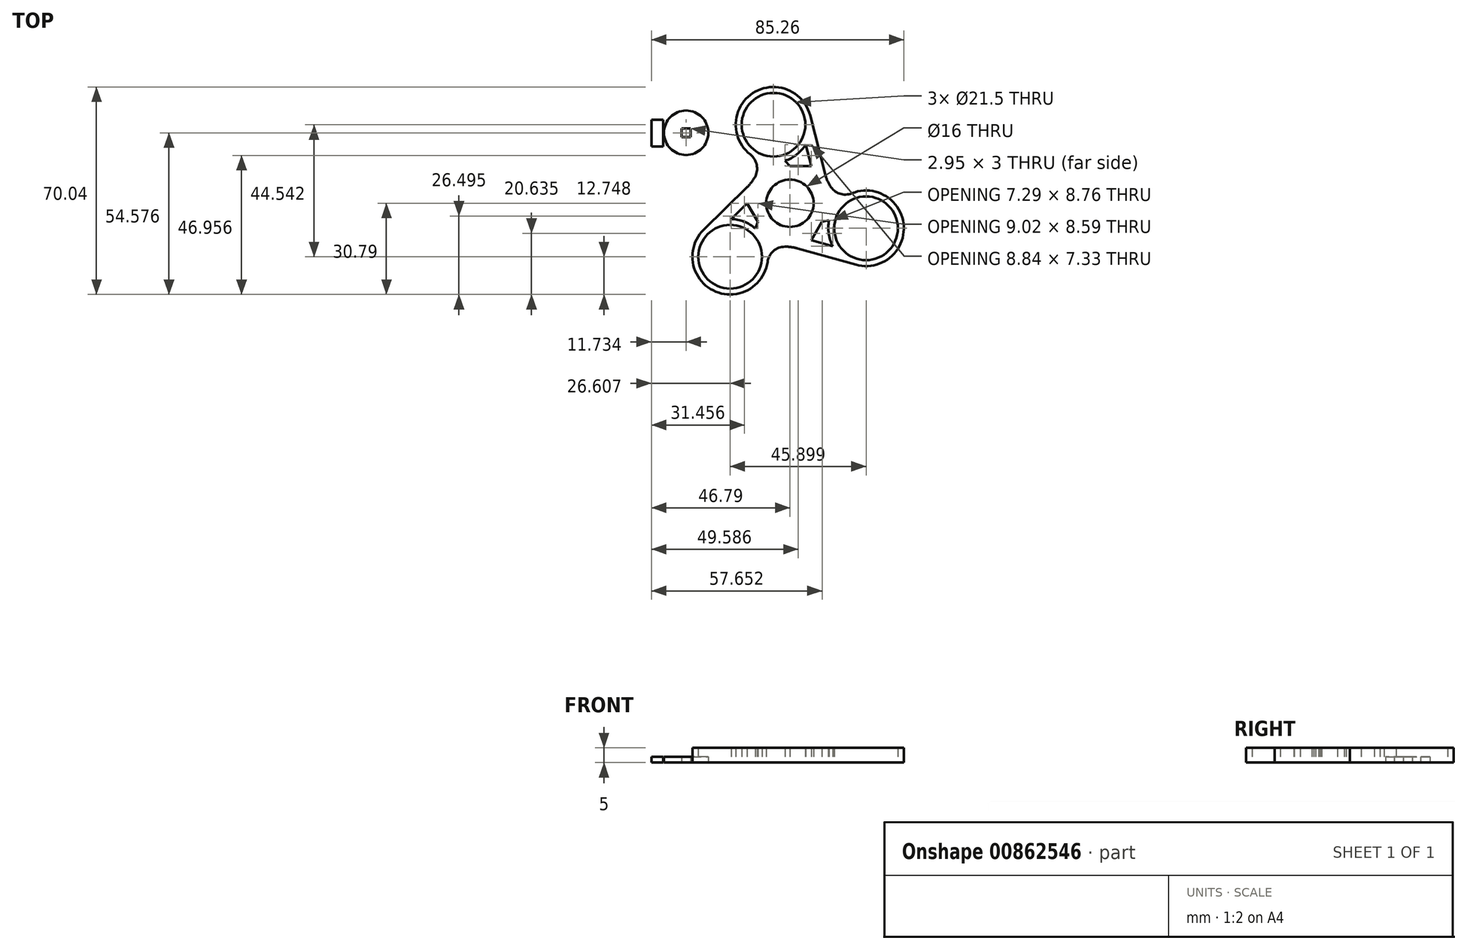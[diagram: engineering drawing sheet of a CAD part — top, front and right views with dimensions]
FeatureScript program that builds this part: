
annotation { "Feature Type Name" : "Feature", "Feature Type Description" : "" }
export const myFeature = defineFeature(function(context is Context, id is Id, definition is map)
    precondition{}
    {
        {
            var Q0;
            Q0=qCreatedBy(makeId("Top.planeOp"),FACE);
            var sketch = newSketch(context, id + "F0", { "sketchPlane" : qUnion([Q0])});
            skCircle(sketch, "E0", {"center": v(0, 0) * mm, "radius": 8 * mm});
            skCircle(sketch, "E1.cCircle", {"center": v(0, 0) * mm, "radius": 12.5 * mm, "construction": true});
            skLineSegment(sketch, "E1.0", {"start": v(-7.22, 12.5) * mm, "end": v(7.22, 12.5) * mm});
            skLineSegment(sketch, "E1.1", {"start": v(7.22, 12.5) * mm, "end": v(14.43, 0) * mm});
            skLineSegment(sketch, "E1.2", {"start": v(14.43, 0) * mm, "end": v(7.22, -12.5) * mm});
            skLineSegment(sketch, "E1.3", {"start": v(7.22, -12.5) * mm, "end": v(-7.22, -12.5) * mm});
            skLineSegment(sketch, "E1.4", {"start": v(-7.22, -12.5) * mm, "end": v(-14.43, 0) * mm});
            skLineSegment(sketch, "E1.5", {"start": v(-14.43, 0) * mm, "end": v(-7.22, 12.5) * mm});
            skPoint(sketch, "E1.0.midPoint", {"position": v(0, 12.5) * mm});
            skLineSegment(sketch, "E2", {"start": v(7.22, 12.5) * mm, "end": v(7.22, 26.5) * mm, "construction": true});
            skArc(sketch, "E3", {"start": v(7.22, 26.5) * mm, "mid": v(-12.8, 36.98) * mm, "end": v(-10, 14.56) * mm});
            skLineSegment(sketch, "E4", {"start": v(-10, 14.56) * mm, "end": v(-7.22, 12.5) * mm});
            skCircle(sketch, "E5", {"center": v(-5.53, 26.5) * mm, "radius": 10.75 * mm});
            skLineSegment(sketch, "E6", {"start": v(14.43, 0) * mm, "end": v(6.82, 29.67) * mm});
            skArc(sketch, "E7", {"start": v(-1.62, 14.36) * mm, "mid": v(2.34, 16.47) * mm, "end": v(5.33, 19.83) * mm});
            skLineSegment(sketch, "E8", {"start": v(-1.62, 14.36) * mm, "end": v(0, 12.5) * mm});
            skLineSegment(sketch, "E9", {"start": v(5.33, 19.83) * mm, "end": v(7.22, 12.5) * mm});
            skSolve(sketch);
        }
        {
            var Q0;
            Q0=makeQuery(id+"F0.imprint","IMPRINT",FACE,{"disambiguationData":[TD([[makeQuery(id+"F0.imprint","IMPRINT",EDGE,{"derivedFrom":sQuery(id+"F0.wireOp",EDGE,"E0")}),-1.0]])]});
            extrude(context, id + "F1", {"entities" : qUnion([Q0]), "depth" : 5 * mm, "offsetDistance" : 25 * mm});
        }
        {
            var Q0;
            Q0=makeQuery(id+"F0.imprint","IMPRINT",FACE,{"disambiguationData":[TD([[makeQuery(id+"F0.imprint","IMPRINT",EDGE,{"derivedFrom":sQuery(id+"F0.wireOp",EDGE,"320d77fd-baf2-4bbf-b8b8-08af1715379d.0")}),1.0]])]});
            var Q1;
            {var subQ0=sQuery(id+"F0.wireOp",EDGE,"f425258b-878d-4473-b1fe-abe1052e9d06.2");var subQ1=sQuery(id+"F0.wireOp",EDGE,"f425258b-878d-4473-b1fe-abe1052e9d06.cCircle");var subQ2=makeQuery(id+"F0.imprint","INTERSECT",VERTEX,{"derivedFrom":[subQ1,subQ0]});Q1=makeQuery(id+"F0.imprint","IMPRINT",FACE,{"disambiguationData":[TD([[makeQuery(id+"F0.imprint","IMPRINT",EDGE,{"disambiguationData":[TD([[subQ2,1.0]])],"derivedFrom":subQ1}),-1.0]])]});}
            var Q2;
            {var subQ0=sQuery(id+"F0.wireOp",EDGE,"f425258b-878d-4473-b1fe-abe1052e9d06.4");var subQ1=sQuery(id+"F0.wireOp",EDGE,"f425258b-878d-4473-b1fe-abe1052e9d06.cCircle");var subQ2=makeQuery(id+"F0.imprint","INTERSECT",VERTEX,{"derivedFrom":[subQ1,subQ0]});Q2=makeQuery(id+"F0.imprint","IMPRINT",FACE,{"disambiguationData":[TD([[makeQuery(id+"F0.imprint","IMPRINT",EDGE,{"disambiguationData":[TD([[subQ2,-1.0]])],"derivedFrom":subQ1}),-1.0]])]});}
            var Q3;
            Q3=makeQuery(id+"F0.imprint","IMPRINT",FACE,{"disambiguationData":[TD([[makeQuery(id+"F0.imprint","IMPRINT",EDGE,{"derivedFrom":sQuery(id+"F0.wireOp",EDGE,"E1.1")}),1.0]])]});
            extrude(context, id + "F2", {"entities" : qUnion([Q0, Q1, Q2, Q3]), "depth" : 5 * mm, "offsetDistance" : 25 * mm});
        }
        {
            var Q0;
            Q0=makeQuery(id+"F2.opExtrude","SWEPT_BODY",BODY,{"disambiguationData":[OSD([sQuery(id+"F0.wireOp",EDGE,"f425258b-878d-4473-b1fe-abe1052e9d06.0"),sQuery(id+"F0.wireOp",EDGE,"f425258b-878d-4473-b1fe-abe1052e9d06.1"),sQuery(id+"F0.wireOp",EDGE,"f425258b-878d-4473-b1fe-abe1052e9d06.2"),sQuery(id+"F0.wireOp",EDGE,"f425258b-878d-4473-b1fe-abe1052e9d06.3"),sQuery(id+"F0.wireOp",EDGE,"f425258b-878d-4473-b1fe-abe1052e9d06.4"),sQuery(id+"F0.wireOp",EDGE,"f425258b-878d-4473-b1fe-abe1052e9d06.5"),sQuery(id+"F0.wireOp",EDGE,"320d77fd-baf2-4bbf-b8b8-08af1715379d.0"),sQuery(id+"F0.wireOp",EDGE,"320d77fd-baf2-4bbf-b8b8-08af1715379d.1"),sQuery(id+"F0.wireOp",EDGE,"320d77fd-baf2-4bbf-b8b8-08af1715379d.2"),sQuery(id+"F0.wireOp",EDGE,"320d77fd-baf2-4bbf-b8b8-08af1715379d.3"),sQuery(id+"F0.wireOp",EDGE,"320d77fd-baf2-4bbf-b8b8-08af1715379d.4"),sQuery(id+"F0.wireOp",EDGE,"320d77fd-baf2-4bbf-b8b8-08af1715379d.5")])]});
            var Q1;
            Q1=makeQuery(id+"F2.opExtrude","SWEPT_BODY",BODY,{"disambiguationData":[OSD([sQuery(id+"F0.wireOp",EDGE,"E1.0"),sQuery(id+"F0.wireOp",EDGE,"E2"),sQuery(id+"F0.wireOp",EDGE,"E3"),sQuery(id+"F0.wireOp",EDGE,"E4"),sQuery(id+"F0.wireOp",EDGE,"E5")])]});
            var Q2;
            Q2=sQuery(id+"F0.wireOp",EDGE,"E1.cCircle");
            circularPattern(context, id + "F3", {"operationType" : NewBodyOperationType.ADD, "entities" : qUnion([Q0, Q1]), "axis" : qUnion([Q2]), "angle" : 360 * degree, "instanceCount" : 3, "equalSpace" : true});
        }
        {
            var Q0;
            Q0=makeQuery(id+"F3.boolean.opBoolean","MERGE",EDGE,{"derivedFrom":[makeQuery(id+"F1.opExtrude","SWEPT_EDGE",EDGE,{"disambiguationData":[OSD([sQuery(id+"F0.wireOp",EDGE,"E1.3"),sQuery(id+"F0.wireOp",EDGE,"E1.4")])]}),makeQuery(id+"F3.opPattern","COPY",EDGE,{"derivedFrom":makeQuery(id+"F2.opExtrude","SWEPT_EDGE",EDGE,{"disambiguationData":[OSD([sQuery(id+"F0.wireOp",EDGE,"E1.0"),sQuery(id+"F0.wireOp",EDGE,"E1.5"),sQuery(id+"F0.wireOp",EDGE,"E4")])]}),"instanceName":"1"})]});
            var Q1;
            {var subQ0=sQuery(id+"F0.wireOp",EDGE,"E4");var subQ1=sQuery(id+"F0.wireOp",EDGE,"E1.5");var subQ2=sQuery(id+"F0.wireOp",EDGE,"E1.0");Q1=makeQuery(id+"F3.boolean.opBoolean","MERGE",EDGE,{"derivedFrom":[makeQuery(id+"F1.opExtrude","SWEPT_EDGE",EDGE,{"disambiguationData":[OSD([subQ2,subQ1,subQ0])]}),makeQuery(id+"F2.opExtrude","SWEPT_EDGE",EDGE,{"disambiguationData":[OSD([subQ2,subQ1,subQ0])]})]});}
            var Q2;
            Q2=makeQuery(id+"F3.boolean.opBoolean","MERGE",EDGE,{"derivedFrom":[makeQuery(id+"F1.opExtrude","SWEPT_EDGE",EDGE,{"disambiguationData":[OSD([sQuery(id+"F0.wireOp",EDGE,"E1.1"),sQuery(id+"F0.wireOp",EDGE,"E1.2")])]}),makeQuery(id+"F3.opPattern","COPY",EDGE,{"derivedFrom":makeQuery(id+"F2.opExtrude","SWEPT_EDGE",EDGE,{"disambiguationData":[OSD([sQuery(id+"F0.wireOp",EDGE,"E1.0"),sQuery(id+"F0.wireOp",EDGE,"E1.5"),sQuery(id+"F0.wireOp",EDGE,"E4")])]}),"instanceName":"2"})]});
            fillet(context, id + "F4", {"entities" : qUnion([Q0, Q1, Q2]), "radius" : 15 * mm, "tangentPropagation" : true, "allowEdgeOverflow" : false});
        }
        {
            var Q0;
            Q0=qCreatedBy(makeId("Top.planeOp"),FACE);
            var sketch = newSketch(context, id + "F5", { "sketchPlane" : qUnion([Q0])});
            skCircle(sketch, "E10", {"center": v(-44.8, 15.18) * mm, "radius": 2.5 * mm, "construction": true});
            skLineSegment(sketch, "E11.bottom", {"start": v(-46.8, 16.68) * mm, "end": v(-42.8, 16.68) * mm});
            skLineSegment(sketch, "E11.top", {"start": v(-46.8, 13.68) * mm, "end": v(-42.8, 13.68) * mm});
            skLineSegment(sketch, "E11.left", {"start": v(-46.8, 16.68) * mm, "end": v(-46.8, 13.68) * mm});
            skLineSegment(sketch, "E11.right", {"start": v(-42.8, 16.68) * mm, "end": v(-42.8, 13.68) * mm});
            skLineSegment(sketch, "E12.bottom", {"start": v(-46.8, 19.18) * mm, "end": v(-42.8, 19.18) * mm});
            skLineSegment(sketch, "E12.top", {"start": v(-46.8, 28.18) * mm, "end": v(-42.8, 28.18) * mm});
            skLineSegment(sketch, "E12.left", {"start": v(-46.8, 19.18) * mm, "end": v(-46.8, 28.18) * mm});
            skLineSegment(sketch, "E12.right", {"start": v(-42.8, 19.18) * mm, "end": v(-42.8, 28.18) * mm});
            skPoint(sketch, "E12.middle", {"position": v(-44.8, 23.68) * mm});
            skCircle(sketch, "E13", {"center": v(-35.06, 23.79) * mm, "radius": 7.5 * mm});
            skLineSegment(sketch, "E14.bottom", {"start": v(-36.53, 25.29) * mm, "end": v(-33.58, 25.29) * mm});
            skLineSegment(sketch, "E14.top", {"start": v(-36.53, 22.29) * mm, "end": v(-33.58, 22.29) * mm});
            skLineSegment(sketch, "E14.left", {"start": v(-36.53, 25.29) * mm, "end": v(-36.53, 22.29) * mm});
            skLineSegment(sketch, "E14.right", {"start": v(-33.58, 25.29) * mm, "end": v(-33.58, 22.29) * mm});
            skSolve(sketch);
        }
        {
            var Q0;
            Q0=makeQuery(id+"F5.imprint","IMPRINT",FACE,{"disambiguationData":[TD([[makeQuery(id+"F5.imprint","IMPRINT",EDGE,{"derivedFrom":sQuery(id+"F5.wireOp",EDGE,"E12.bottom")}),1.0]])]});
            var Q1;
            Q1=makeQuery(id+"F5.imprint","IMPRINT",FACE,{"disambiguationData":[TD([[makeQuery(id+"F5.imprint","IMPRINT",EDGE,{"derivedFrom":sQuery(id+"F5.wireOp",EDGE,"E13")}),1.0]])]});
            extrude(context, id + "F6", {"entities" : qUnion([Q0, Q1]), "depth" : 2 * mm, "offsetDistance" : 25 * mm});
        }
        {
            var Q0;
            {var subQ0=sQuery(id+"F0.wireOp",EDGE,"E4");var subQ1=sQuery(id+"F0.wireOp",EDGE,"E1.5");var subQ2=sQuery(id+"F0.wireOp",EDGE,"E1.0");Q0=makeQuery(id+"F4.opFillet","BLEND_EDGE",EDGE,{"blendedFrom":[makeQuery(id+"F3.boolean.opBoolean","MERGE",EDGE,{"derivedFrom":[makeQuery(id+"F1.opExtrude","SWEPT_EDGE",EDGE,{"disambiguationData":[OSD([subQ2,subQ1,subQ0])]}),makeQuery(id+"F2.opExtrude","SWEPT_EDGE",EDGE,{"disambiguationData":[OSD([subQ2,subQ1,subQ0])]})]}),makeQuery(id+"F2.opExtrude","SWEPT_FACE",FACE,{"disambiguationData":[OSD([sQuery(id+"F0.wireOp",EDGE,"E3")])]})],"blendedInto":[makeQuery(id+"F2.opExtrude","SWEPT_FACE",FACE,{"disambiguationData":[OSD([sQuery(id+"F0.wireOp",EDGE,"E3")])]})]});}
            var Q1;
            Q1=makeQuery(id+"F4.opFillet","BLEND_EDGE",EDGE,{"blendedFrom":[makeQuery(id+"F3.boolean.opBoolean","MERGE",EDGE,{"derivedFrom":[makeQuery(id+"F1.opExtrude","SWEPT_EDGE",EDGE,{"disambiguationData":[OSD([sQuery(id+"F0.wireOp",EDGE,"E1.1"),sQuery(id+"F0.wireOp",EDGE,"E1.2")])]}),makeQuery(id+"F3.opPattern","COPY",EDGE,{"derivedFrom":makeQuery(id+"F2.opExtrude","SWEPT_EDGE",EDGE,{"disambiguationData":[OSD([sQuery(id+"F0.wireOp",EDGE,"E1.0"),sQuery(id+"F0.wireOp",EDGE,"E1.5"),sQuery(id+"F0.wireOp",EDGE,"E4")])]}),"instanceName":"2"})]}),makeQuery(id+"F3.opPattern","COPY",FACE,{"derivedFrom":makeQuery(id+"F2.opExtrude","SWEPT_FACE",FACE,{"disambiguationData":[OSD([sQuery(id+"F0.wireOp",EDGE,"E3")])]}),"instanceName":"2"})],"blendedInto":[makeQuery(id+"F3.opPattern","COPY",FACE,{"derivedFrom":makeQuery(id+"F2.opExtrude","SWEPT_FACE",FACE,{"disambiguationData":[OSD([sQuery(id+"F0.wireOp",EDGE,"E3")])]}),"instanceName":"2"})]});
            var Q2;
            Q2=makeQuery(id+"F4.opFillet","BLEND_EDGE",EDGE,{"blendedFrom":[makeQuery(id+"F3.boolean.opBoolean","MERGE",EDGE,{"derivedFrom":[makeQuery(id+"F1.opExtrude","SWEPT_EDGE",EDGE,{"disambiguationData":[OSD([sQuery(id+"F0.wireOp",EDGE,"E1.3"),sQuery(id+"F0.wireOp",EDGE,"E1.4")])]}),makeQuery(id+"F3.opPattern","COPY",EDGE,{"derivedFrom":makeQuery(id+"F2.opExtrude","SWEPT_EDGE",EDGE,{"disambiguationData":[OSD([sQuery(id+"F0.wireOp",EDGE,"E1.0"),sQuery(id+"F0.wireOp",EDGE,"E1.5"),sQuery(id+"F0.wireOp",EDGE,"E4")])]}),"instanceName":"1"})]}),makeQuery(id+"F3.opPattern","COPY",FACE,{"derivedFrom":makeQuery(id+"F2.opExtrude","SWEPT_FACE",FACE,{"disambiguationData":[OSD([sQuery(id+"F0.wireOp",EDGE,"E3")])]}),"instanceName":"1"})],"blendedInto":[makeQuery(id+"F3.opPattern","COPY",FACE,{"derivedFrom":makeQuery(id+"F2.opExtrude","SWEPT_FACE",FACE,{"disambiguationData":[OSD([sQuery(id+"F0.wireOp",EDGE,"E3")])]}),"instanceName":"1"})]});
            fillet(context, id + "F7", {"entities" : qUnion([Q0, Q1, Q2]), "radius" : 6 * mm, "tangentPropagation" : true, "allowEdgeOverflow" : false});
        }
    });
